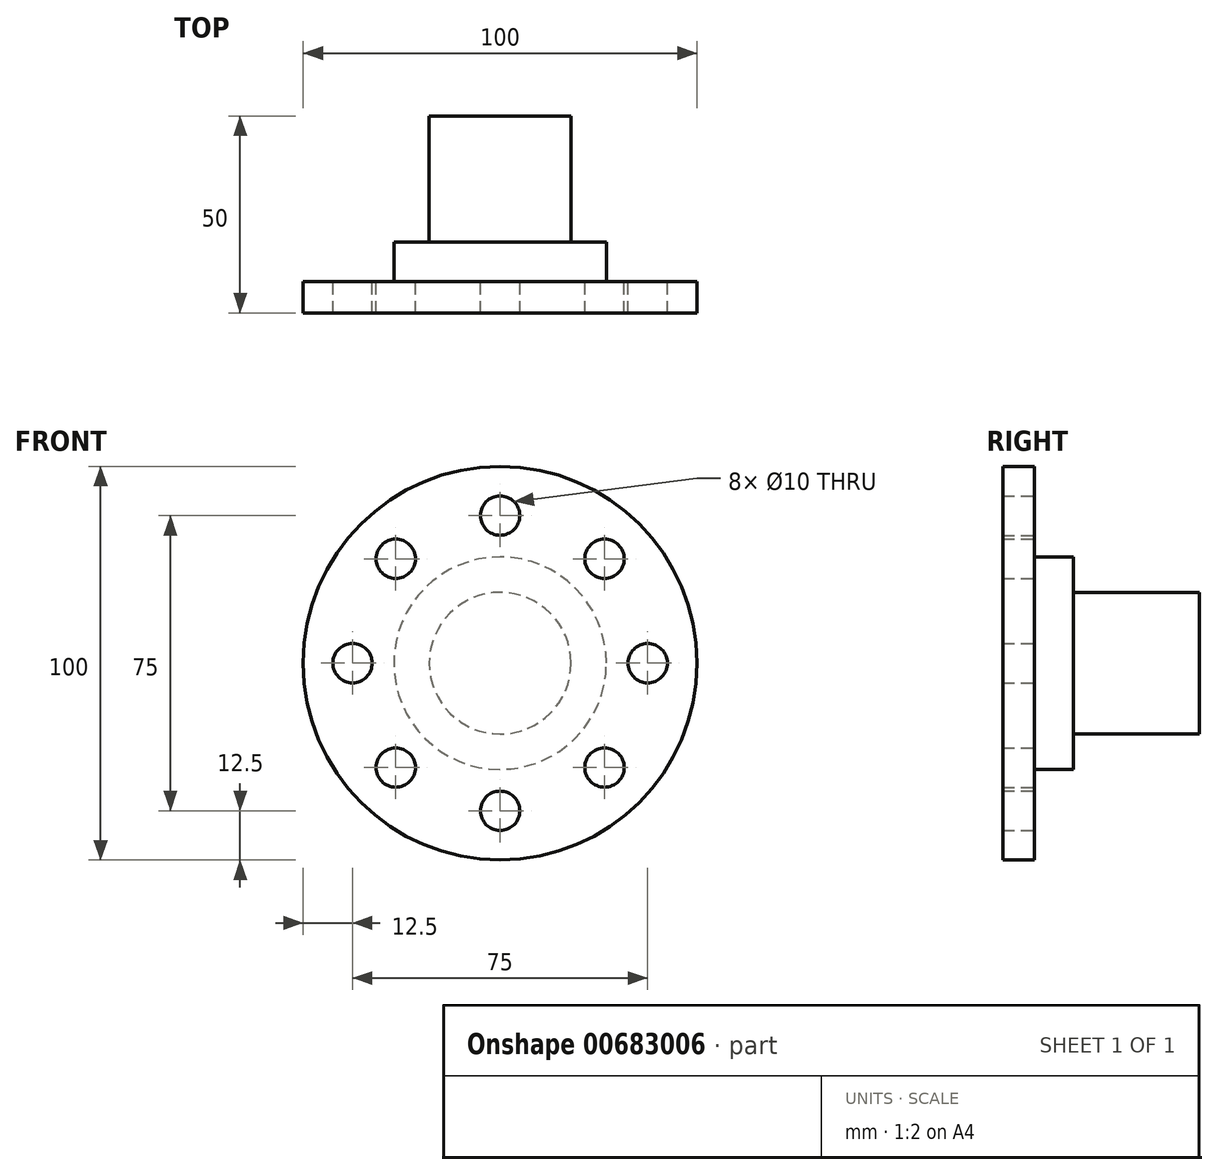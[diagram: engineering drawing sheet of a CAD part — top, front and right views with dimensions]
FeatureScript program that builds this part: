
annotation { "Feature Type Name" : "Feature", "Feature Type Description" : "" }
export const myFeature = defineFeature(function(context is Context, id is Id, definition is map)
    precondition{}
    {
        {
            var Q0;
            Q0=qCreatedBy(makeId("Front.planeOp"),FACE);
            var sketch = newSketch(context, id + "F0", { "sketchPlane" : qUnion([Q0])});
            skCircle(sketch, "E0", {"center": v(0, 0) * mm, "radius": 50 * mm});
            skCircle(sketch, "E1", {"center": v(0, 0) * mm, "radius": 37.5 * mm, "construction": true});
            skCircle(sketch, "E2", {"center": v(0, 37.5) * mm, "radius": 5 * mm});
            skCircle(sketch, "E3.1.0", {"center": v(-26.52, 26.52) * mm, "radius": 5 * mm});
            skCircle(sketch, "E3.2.0", {"center": v(-37.5, 0) * mm, "radius": 5 * mm});
            skCircle(sketch, "E3.3.0", {"center": v(-26.52, -26.52) * mm, "radius": 5 * mm});
            skCircle(sketch, "E3.4.0", {"center": v(0, -37.5) * mm, "radius": 5 * mm});
            skCircle(sketch, "E3.5.0", {"center": v(26.52, -26.52) * mm, "radius": 5 * mm});
            skCircle(sketch, "E3.6.0", {"center": v(37.5, 0) * mm, "radius": 5 * mm});
            skCircle(sketch, "E3.7.0", {"center": v(26.52, 26.52) * mm, "radius": 5 * mm});
            skSolve(sketch);
        }
        {
            var Q0;
            Q0 = qSketchRegion(id + "F0", true);
            extrude(context, id + "F1", {"entities" : qUnion([Q0]), "depth" : 8 * mm, "offsetDistance" : 25 * mm});
        }
        {
            var Q0;
            Q0=makeQuery(id+"F1.opExtrude","CAP_FACE",FACE,{"disambiguationData":[OSD([sQuery(id+"F0.wireOp",EDGE,"E0"),sQuery(id+"F0.wireOp",EDGE,"E2"),sQuery(id+"F0.wireOp",EDGE,"E3.1.0"),sQuery(id+"F0.wireOp",EDGE,"E3.2.0"),sQuery(id+"F0.wireOp",EDGE,"E3.3.0"),sQuery(id+"F0.wireOp",EDGE,"E3.4.0"),sQuery(id+"F0.wireOp",EDGE,"E3.5.0"),sQuery(id+"F0.wireOp",EDGE,"E3.6.0"),sQuery(id+"F0.wireOp",EDGE,"E3.7.0")])],"isStart":true});
            var sketch = newSketch(context, id + "F2", { "sketchPlane" : qUnion([Q0])});
            skCircle(sketch, "E4", {"center": v(0, 0) * mm, "radius": 27 * mm});
            skSolve(sketch);
        }
        {
            var Q0;
            Q0 = qSketchRegion(id + "F2", true);
            extrude(context, id + "F3", {"entities" : qUnion([Q0]), "operationType" : NewBodyOperationType.ADD, "depth" : 10 * mm, "offsetDistance" : 25 * mm});
        }
        {
            var Q0;
            Q0=makeQuery(id+"F3.opExtrude","CAP_FACE",FACE,{"disambiguationData":[OSD([sQuery(id+"F2.wireOp",EDGE,"E4")])],"isStart":false});
            var sketch = newSketch(context, id + "F4", { "sketchPlane" : qUnion([Q0])});
            skCircle(sketch, "E5", {"center": v(0, 0) * mm, "radius": 18 * mm});
            skSolve(sketch);
        }
        {
            var Q0;
            Q0 = qSketchRegion(id + "F4", true);
            extrude(context, id + "F5", {"entities" : qUnion([Q0]), "operationType" : NewBodyOperationType.ADD, "depth" : 32 * mm, "offsetDistance" : 25 * mm});
        }
    });
